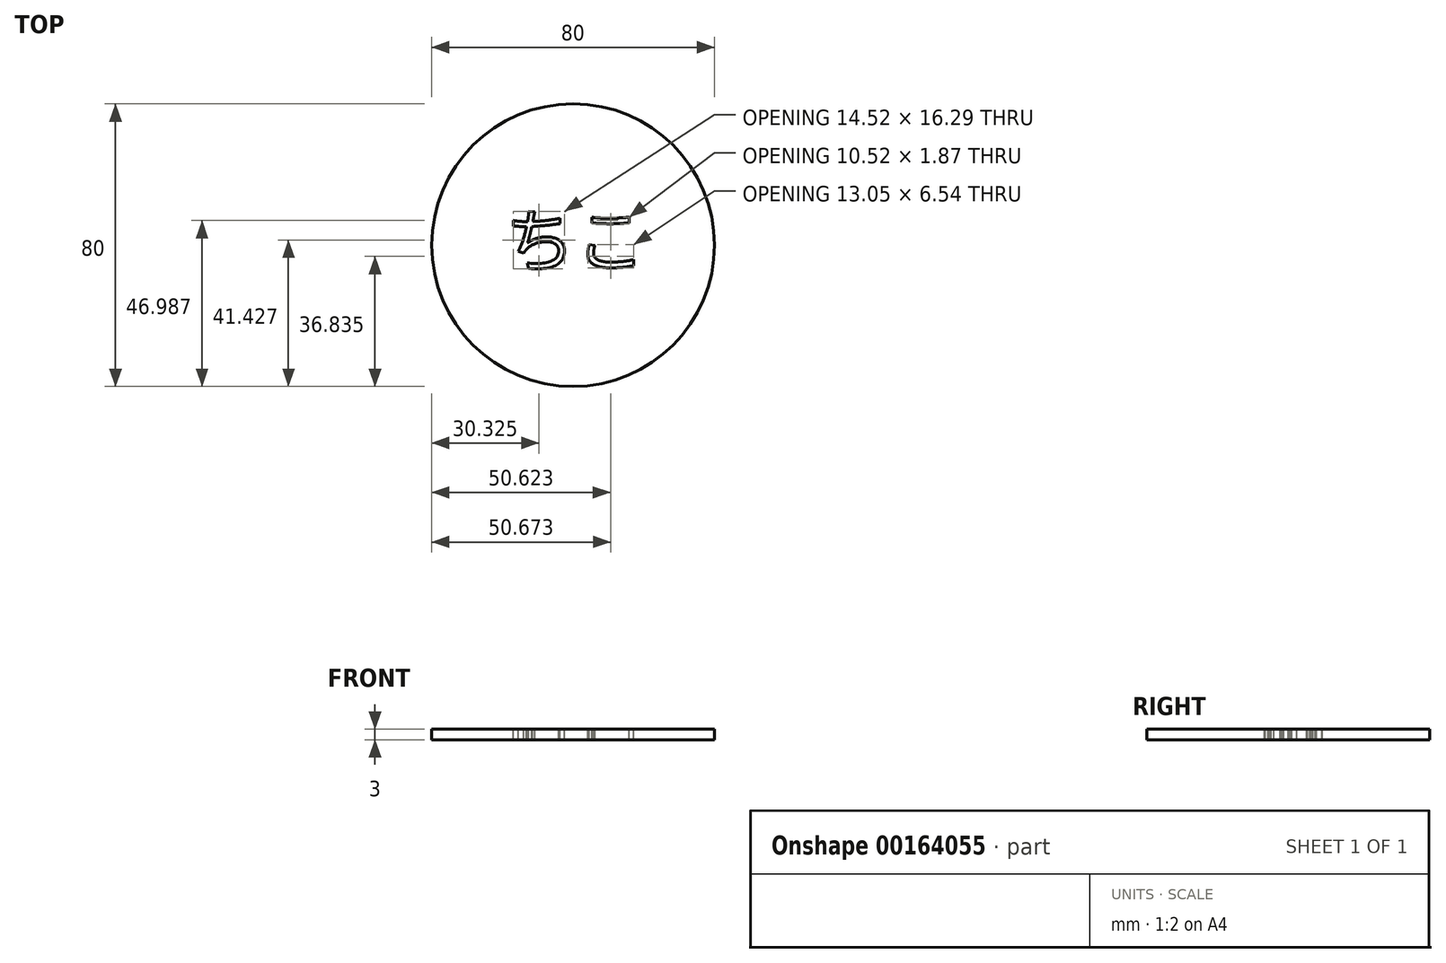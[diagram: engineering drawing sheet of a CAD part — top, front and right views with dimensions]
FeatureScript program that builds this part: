
annotation { "Feature Type Name" : "Feature", "Feature Type Description" : "" }
export const myFeature = defineFeature(function(context is Context, id is Id, definition is map)
    precondition{}
    {
        {
            var Q0;
            Q0=qCreatedBy(makeId("Top.planeOp"),FACE);
            var sketch = newSketch(context, id + "F0", { "sketchPlane" : qUnion([Q0])});
            skCircle(sketch, "E0", {"center": v(0, 0) * mm, "radius": 40 * mm});
            skText(sketch, "E1", { "text": "ちこ", "fontName": "NotoSansCJKjp-Regular.otf"});
            const initialGuessF0  = {"E1": [-0.01924, -0.00604, 1, 0, 0.01432]};
            skSetInitialGuess(sketch, initialGuessF0);
            skSolve(sketch);
        }
        {
            var Q0;
            Q0=makeQuery(id+"F0.imprint","IMPRINT",FACE,{"disambiguationData":[TD([[makeQuery(id+"F0.imprint","IMPRINT",EDGE,{"derivedFrom":sQuery(id+"F0.wireOp",EDGE,"E0")}),1.0]])]});
            extrude(context, id + "F1", {"entities" : qUnion([Q0]), "oppositeDirection" : true, "depth" : 3 * mm});
        }
    });
